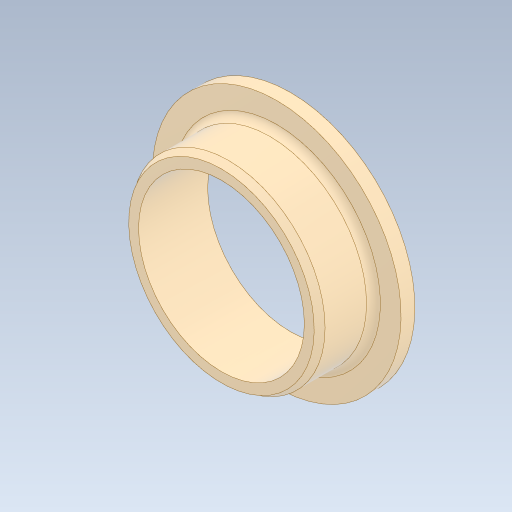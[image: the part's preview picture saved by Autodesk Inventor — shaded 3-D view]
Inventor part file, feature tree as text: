
AUTODESK INVENTOR PART (.ipt)
format: ipt  version: 2024 (Build 280153000, 153)  size: 148,992 bytes
history: native  units: mm
features: other x1, revolve x1, chamfer x1, fillet x1, sketch x1
ambient origin geometry x8: Origin, YZ Plane, XZ Plane, XY Plane, X Axis, Y Axis, Z Axis, Center Point
bodies: Body1 (feature_tree)
feature tree (5):
  other  "ソリッド1"
  revolve  "回転1"
  chamfer  "面取り1"  Distance=12.0mm
  fillet  "フィレット2"  Radius=14.0mm
  sketch  "スケッチ1"
